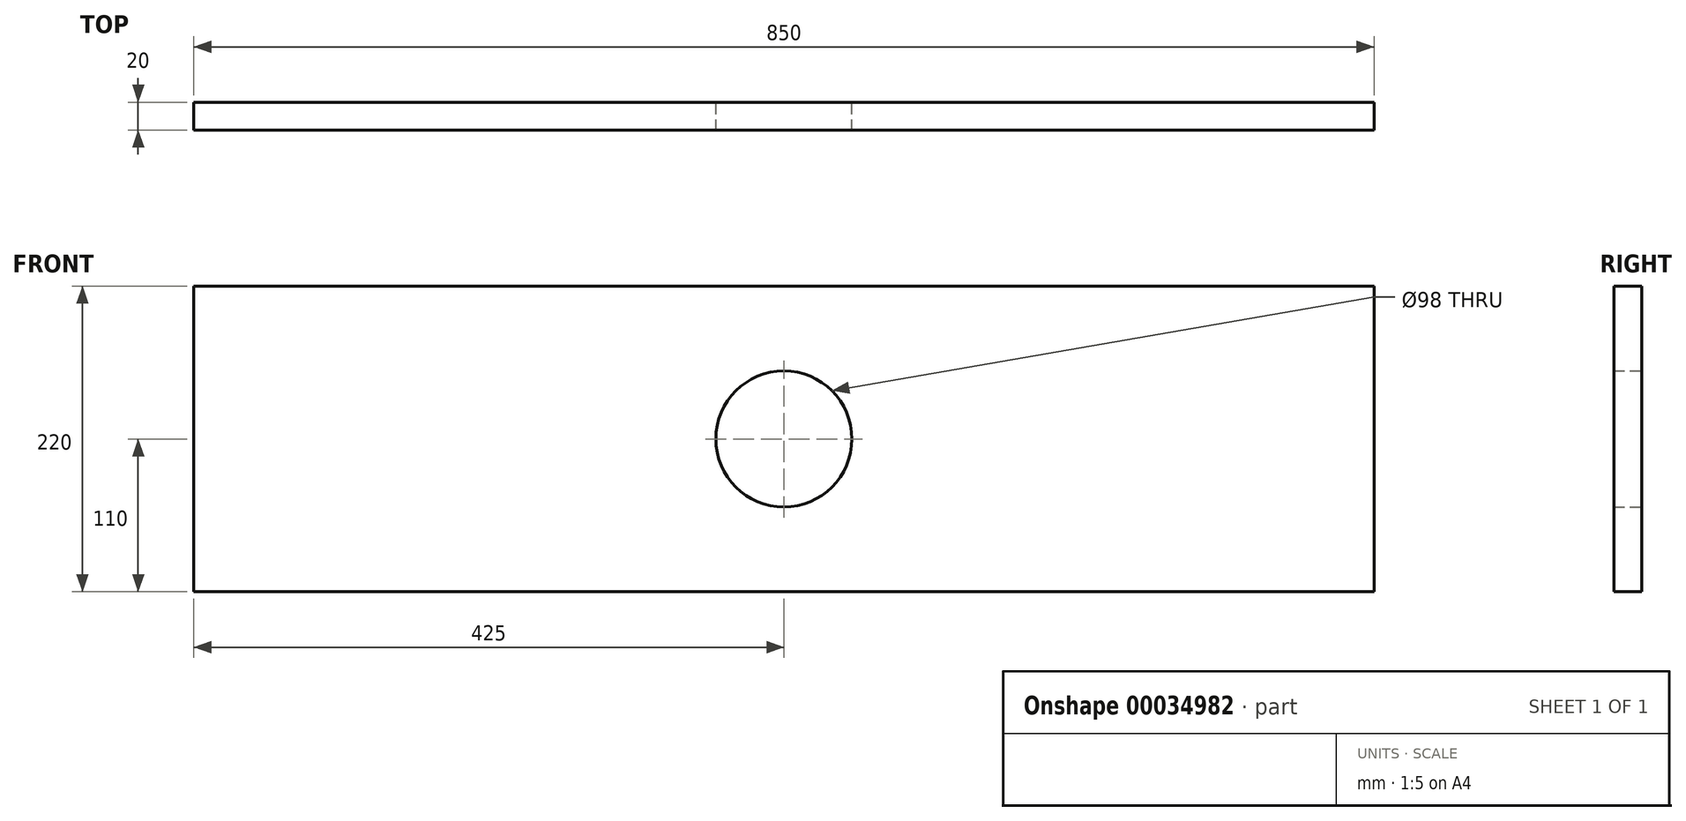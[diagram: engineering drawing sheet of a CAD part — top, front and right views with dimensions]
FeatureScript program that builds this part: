
annotation { "Feature Type Name" : "Feature", "Feature Type Description" : "" }
export const myFeature = defineFeature(function(context is Context, id is Id, definition is map)
    precondition{}
    {
        {
            var Q0;
            Q0=qCreatedBy(makeId("Front.planeOp"),FACE);
            var sketch = newSketch(context, id + "F0", { "sketchPlane" : qUnion([Q0])});
            skLineSegment(sketch, "E0.bottom", {"start": v(0, 0) * mm, "end": v(850, 0) * mm});
            skLineSegment(sketch, "E0.top", {"start": v(0, 220) * mm, "end": v(850, 220) * mm});
            skLineSegment(sketch, "E0.left", {"start": v(0, 0) * mm, "end": v(0, 220) * mm});
            skLineSegment(sketch, "E0.right", {"start": v(850, 0) * mm, "end": v(850, 220) * mm});
            skCircle(sketch, "E1", {"center": v(425, 110) * mm, "radius": 49 * mm});
            skSolve(sketch);
        }
        {
            var Q0;
            Q0=makeQuery(id+"F0.imprint","IMPRINT",FACE,{"disambiguationData":[TD([[makeQuery(id+"F0.imprint","IMPRINT",EDGE,{"derivedFrom":sQuery(id+"F0.wireOp",EDGE,"E0.bottom")}),1.0]])]});
            extrude(context, id + "F1", {"entities" : qUnion([Q0]), "depth" : 20 * mm});
        }
    });
